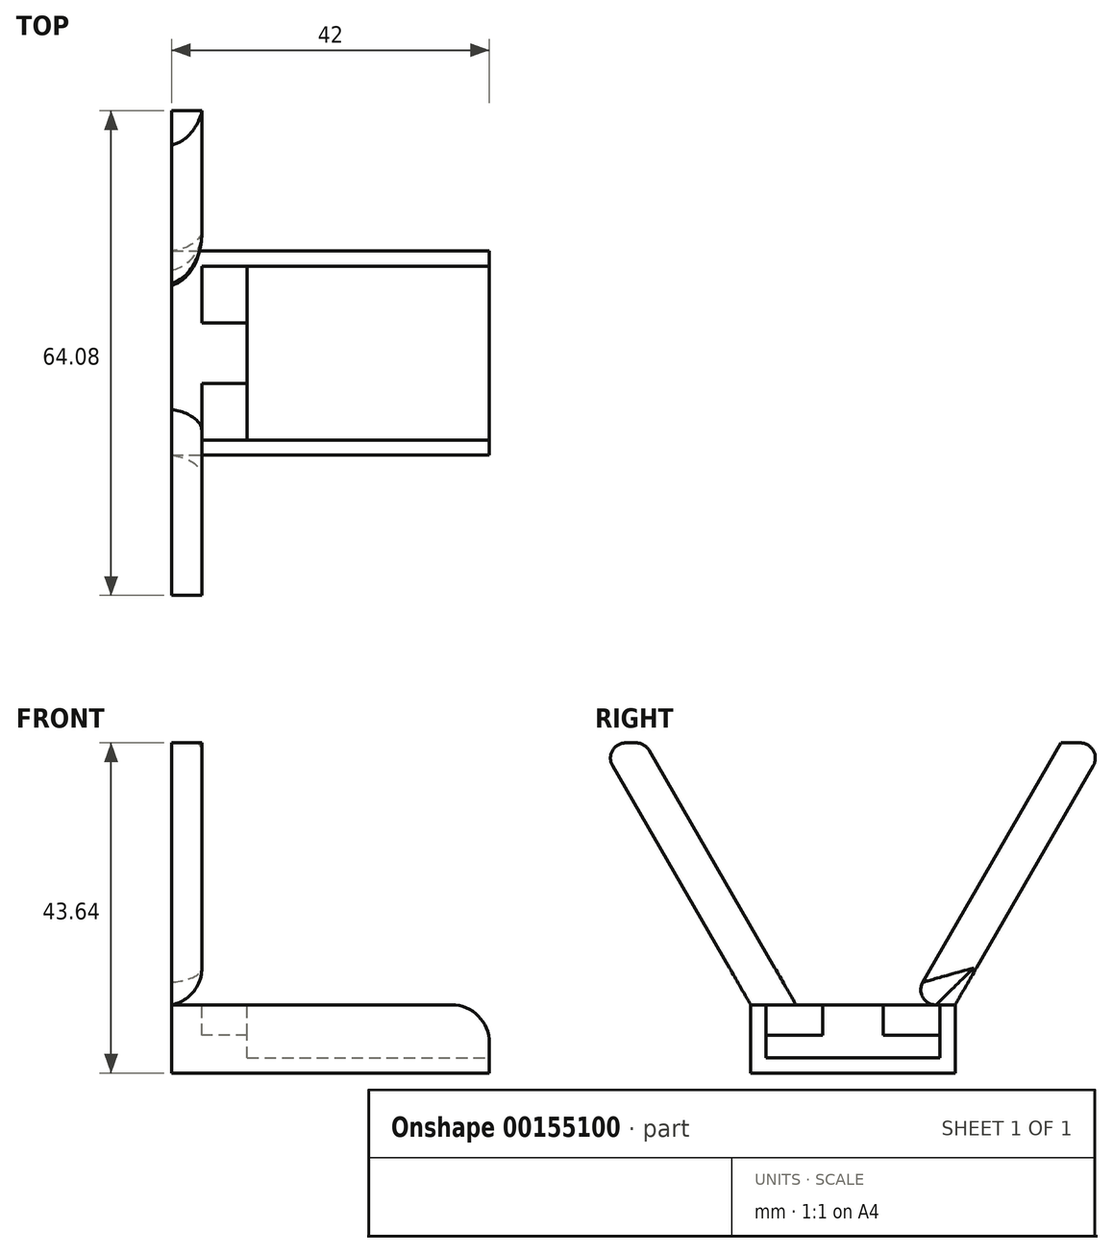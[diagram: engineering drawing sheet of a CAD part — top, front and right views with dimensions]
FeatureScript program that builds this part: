
annotation { "Feature Type Name" : "Feature", "Feature Type Description" : "" }
export const myFeature = defineFeature(function(context is Context, id is Id, definition is map)
    precondition{}
    {
        {
            var Q0;
            Q0=qCreatedBy(makeId("Top.planeOp"),FACE);
            var sketch = newSketch(context, id + "F0", { "sketchPlane" : qUnion([Q0])});
            skLineSegment(sketch, "E0.bottom", {"start": v(-21, 13.5) * mm, "end": v(21, 13.5) * mm});
            skLineSegment(sketch, "E0.top", {"start": v(-21, -13.5) * mm, "end": v(21, -13.5) * mm});
            skLineSegment(sketch, "E0.left", {"start": v(-21, 13.5) * mm, "end": v(-21, -13.5) * mm});
            skLineSegment(sketch, "E0.right", {"start": v(21, 13.5) * mm, "end": v(21, -13.5) * mm});
            skSolve(sketch);
        }
        {
            var Q0;
            Q0=qSketchRegion(id+"F0",true);
            extrude(context, id + "F1", {"entities" : qUnion([Q0]), "oppositeDirection" : true, "depth" : 9 * mm});
        }
        {
            var Q0;
            Q0=qCreatedBy(makeId("Top.planeOp"),FACE);
            var sketch = newSketch(context, id + "F2", { "sketchPlane" : qUnion([Q0])});
            skLineSegment(sketch, "E1.bottom", {"start": v(-11, 11.5) * mm, "end": v(21, 11.5) * mm});
            skLineSegment(sketch, "E1.top", {"start": v(-11, -11.5) * mm, "end": v(21, -11.5) * mm});
            skLineSegment(sketch, "E1.left", {"start": v(-11, 11.5) * mm, "end": v(-11, -11.5) * mm});
            skLineSegment(sketch, "E1.right", {"start": v(21, 11.5) * mm, "end": v(21, -11.5) * mm});
            skSolve(sketch);
        }
        {
            var Q0;
            Q0=qSketchRegion(id+"F2",true);
            extrude(context, id + "F3", {"entities" : qUnion([Q0]), "oppositeDirection" : true, "depth" : 7 * mm});
        }
        {
            var Q0;
            Q0=makeQuery(id+"F3.opExtrude","SWEPT_BODY",BODY,{"disambiguationData":[OSD([sQuery(id+"F2.wireOp",EDGE,"E1.bottom"),sQuery(id+"F2.wireOp",EDGE,"E1.top"),sQuery(id+"F2.wireOp",EDGE,"E1.left"),sQuery(id+"F2.wireOp",EDGE,"E1.right")])]});
            var Q1;
            Q1=makeQuery(id+"F1.opExtrude","SWEPT_BODY",BODY,{"disambiguationData":[OSD([sQuery(id+"F0.wireOp",EDGE,"E0.bottom"),sQuery(id+"F0.wireOp",EDGE,"E0.top"),sQuery(id+"F0.wireOp",EDGE,"E0.left"),sQuery(id+"F0.wireOp",EDGE,"E0.right")])]});
            booleanBodies(context, id + "F4", {"operationType" : BooleanOperationType.SUBTRACTION, "tools" : qUnion([Q0]), "targets" : qUnion([Q1])});
        }
        {
            var Q0;
            Q0=qCreatedBy(makeId("Top.planeOp"),FACE);
            var sketch = newSketch(context, id + "F5", { "sketchPlane" : qUnion([Q0])});
            skLineSegment(sketch, "E2.bottom", {"start": v(-11, 11.5) * mm, "end": v(-17, 11.5) * mm});
            skLineSegment(sketch, "E2.top", {"start": v(-11, 4) * mm, "end": v(-17, 4) * mm});
            skLineSegment(sketch, "E2.left", {"start": v(-11, 11.5) * mm, "end": v(-11, 4) * mm});
            skLineSegment(sketch, "E2.right", {"start": v(-17, 11.5) * mm, "end": v(-17, 4) * mm});
            skSolve(sketch);
        }
        {
            var Q0;
            Q0=qCreatedBy(makeId("Top.planeOp"),FACE);
            var sketch = newSketch(context, id + "F6", { "sketchPlane" : qUnion([Q0])});
            skLineSegment(sketch, "E3.bottom", {"start": v(-11, -4) * mm, "end": v(-17, -4) * mm});
            skLineSegment(sketch, "E3.top", {"start": v(-11, -11.5) * mm, "end": v(-17, -11.5) * mm});
            skLineSegment(sketch, "E3.left", {"start": v(-11, -4) * mm, "end": v(-11, -11.5) * mm});
            skLineSegment(sketch, "E3.right", {"start": v(-17, -4) * mm, "end": v(-17, -11.5) * mm});
            skSolve(sketch);
        }
        {
            var Q0;
            Q0=qSketchRegion(id+"F6",true);
            var Q1;
            Q1=qSketchRegion(id+"F5",true);
            extrude(context, id + "F7", {"entities" : qUnion([Q0, Q1]), "oppositeDirection" : true, "depth" : 4 * mm});
        }
        {
            var Q0;
            Q0=makeQuery(id+"F7.opExtrude","SWEPT_BODY",BODY,{"disambiguationData":[OSD([sQuery(id+"F5.wireOp",EDGE,"E2.bottom"),sQuery(id+"F5.wireOp",EDGE,"E2.top"),sQuery(id+"F5.wireOp",EDGE,"E2.left"),sQuery(id+"F5.wireOp",EDGE,"E2.right")])]});
            var Q1;
            Q1=makeQuery(id+"F7.opExtrude","SWEPT_BODY",BODY,{"disambiguationData":[OSD([sQuery(id+"F6.wireOp",EDGE,"E3.bottom"),sQuery(id+"F6.wireOp",EDGE,"E3.top"),sQuery(id+"F6.wireOp",EDGE,"E3.left"),sQuery(id+"F6.wireOp",EDGE,"E3.right")])]});
            var Q2;
            Q2=makeQuery(id+"F1.opExtrude","SWEPT_BODY",BODY,{"disambiguationData":[OSD([sQuery(id+"F0.wireOp",EDGE,"E0.bottom"),sQuery(id+"F0.wireOp",EDGE,"E0.top"),sQuery(id+"F0.wireOp",EDGE,"E0.left"),sQuery(id+"F0.wireOp",EDGE,"E0.right")])]});
            booleanBodies(context, id + "F8", {"operationType" : BooleanOperationType.SUBTRACTION, "tools" : qUnion([Q0, Q1]), "targets" : qUnion([Q2])});
        }
        {
            var Q0;
            Q0=makeQuery(id+"F1.opExtrude","SWEPT_FACE",FACE,{"disambiguationData":[OSD([sQuery(id+"F0.wireOp",EDGE,"E0.left")])]});
            var sketch = newSketch(context, id + "F9", { "sketchPlane" : qUnion([Q0])});
            skLineSegment(sketch, "E4", {"start": v(13.5, 0) * mm, "end": v(33.5, 34.64) * mm});
            skLineSegment(sketch, "E5", {"start": v(33.5, 34.64) * mm, "end": v(-33.5, 34.64) * mm});
            skLineSegment(sketch, "E6", {"start": v(-33.5, 34.64) * mm, "end": v(-13.5, 0) * mm});
            skLineSegment(sketch, "E7", {"start": v(-13.5, 0) * mm, "end": v(13.5, 0) * mm});
            skSolve(sketch);
        }
        {
            var Q0;
            Q0=qSketchRegion(id+"F9",true);
            extrude(context, id + "F10", {"entities" : qUnion([Q0]), "oppositeDirection" : true, "depth" : 4 * mm});
        }
        {
            var Q0;
            Q0=makeQuery(id+"F9.imprint","IMPRINT",FACE,{"disambiguationData":[TD([[makeQuery(id+"F9.imprint","IMPRINT",EDGE,{"derivedFrom":sQuery(id+"F9.wireOp",EDGE,"E4")}),1.0]])]});
            var sketch = newSketch(context, id + "F11", { "sketchPlane" : qUnion([Q0])});
            skLineSegment(sketch, "E8", {"start": v(7.5, 0) * mm, "end": v(27.5, 34.64) * mm});
            skLineSegment(sketch, "E9", {"start": v(27.5, 34.64) * mm, "end": v(-27.5, 34.64) * mm});
            skLineSegment(sketch, "E10", {"start": v(-27.5, 34.64) * mm, "end": v(-7.5, 0) * mm});
            skLineSegment(sketch, "E11", {"start": v(-7.5, 0) * mm, "end": v(7.5, 0) * mm});
            skSolve(sketch);
        }
        {
            var Q0;
            Q0=qSketchRegion(id+"F11",true);
            extrude(context, id + "F12", {"entities" : qUnion([Q0]), "oppositeDirection" : true, "depth" : 5 * mm});
        }
        {
            var Q0;
            Q0=makeQuery(id+"F12.opExtrude","SWEPT_BODY",BODY,{"disambiguationData":[OSD([sQuery(id+"F11.wireOp",EDGE,"E8"),sQuery(id+"F11.wireOp",EDGE,"E9"),sQuery(id+"F11.wireOp",EDGE,"E10"),sQuery(id+"F11.wireOp",EDGE,"E11")])]});
            var Q1;
            Q1=makeQuery(id+"F10.opExtrude","SWEPT_BODY",BODY,{"disambiguationData":[OSD([sQuery(id+"F9.wireOp",EDGE,"E4"),sQuery(id+"F9.wireOp",EDGE,"E5"),sQuery(id+"F9.wireOp",EDGE,"E6"),sQuery(id+"F9.wireOp",EDGE,"E7")])]});
            booleanBodies(context, id + "F13", {"operationType" : BooleanOperationType.SUBTRACTION, "tools" : qUnion([Q0]), "targets" : qUnion([Q1])});
        }
        {
            var Q0;
            Q0=makeQuery(id+"F10.opExtrude","SWEPT_EDGE",EDGE,{"disambiguationData":[OSD([sQuery(id+"F9.wireOp",EDGE,"E5"),sQuery(id+"F9.wireOp",EDGE,"E6")])]});
            var Q1;
            Q1=makeQuery(id+"F13.opBoolean","COPY",EDGE,{"derivedFrom":makeQuery(id+"F12.opExtrude","SWEPT_EDGE",EDGE,{"disambiguationData":[OSD([sQuery(id+"F9.wireOp",EDGE,"E5"),sQuery(id+"F11.wireOp",EDGE,"E9"),sQuery(id+"F11.wireOp",EDGE,"E10")])]})});
            var Q2;
            Q2=makeQuery(id+"F13.opBoolean","COPY",EDGE,{"derivedFrom":makeQuery(id+"F12.opExtrude","SWEPT_EDGE",EDGE,{"disambiguationData":[OSD([sQuery(id+"F9.wireOp",EDGE,"E5"),sQuery(id+"F11.wireOp",EDGE,"E8"),sQuery(id+"F11.wireOp",EDGE,"E9")])]})});
            var Q3;
            Q3=makeQuery(id+"F10.opExtrude","SWEPT_EDGE",EDGE,{"disambiguationData":[OSD([sQuery(id+"F9.wireOp",EDGE,"E4"),sQuery(id+"F9.wireOp",EDGE,"E5")])]});
            var Q4;
            Q4=makeQuery(id+"F13.opBoolean","COPY",EDGE,{"derivedFrom":makeQuery(id+"F12.opExtrude","SWEPT_EDGE",EDGE,{"disambiguationData":[OSD([sQuery(id+"F9.wireOp",EDGE,"E7"),sQuery(id+"F11.wireOp",EDGE,"E8"),sQuery(id+"F11.wireOp",EDGE,"E11")])]})});
            var Q5;
            Q5=makeQuery(id+"F13.opBoolean","COPY",EDGE,{"derivedFrom":makeQuery(id+"F12.opExtrude","SWEPT_EDGE",EDGE,{"disambiguationData":[OSD([sQuery(id+"F9.wireOp",EDGE,"E7"),sQuery(id+"F11.wireOp",EDGE,"E10"),sQuery(id+"F11.wireOp",EDGE,"E11")])]})});
            var Q6;
            Q6=makeQuery(id+"F4.opBoolean","COPY",EDGE,{"derivedFrom":makeQuery(id+"F3.opExtrude","CAP_EDGE",EDGE,{"disambiguationData":[OSD([sQuery(id+"F2.wireOp",EDGE,"E1.left")])],"isStart":true})});
            var Q7;
            Q7=makeQuery(id+"F8.opBoolean","COPY",EDGE,{"derivedFrom":makeQuery(id+"F7.opExtrude","CAP_EDGE",EDGE,{"disambiguationData":[OSD([sQuery(id+"F5.wireOp",EDGE,"E2.left")])],"isStart":false})});
            var Q8;
            Q8=makeQuery(id+"F8.opBoolean","COPY",EDGE,{"derivedFrom":makeQuery(id+"F7.opExtrude","CAP_EDGE",EDGE,{"disambiguationData":[OSD([sQuery(id+"F6.wireOp",EDGE,"E3.left")])],"isStart":false})});
            fillet(context, id + "F14", {"entities" : qUnion([Q0, Q1, Q2, Q3, Q4, Q5, Q6, Q7, Q8]), "radius" : 2 * mm, "tangentPropagation" : true, "allowEdgeOverflow" : false});
        }
        {
            var Q0;
            {var subQ0=sQuery(id+"F9.wireOp",EDGE,"E4");var subQ1=sQuery(id+"F9.wireOp",EDGE,"E7");Q0=makeQuery(id+"F13.opBoolean","SPLIT",EDGE,{"disambiguationData":[TD([makeQuery(id+"F10.opExtrude","SWEPT_FACE",FACE,{"disambiguationData":[OSD([subQ0])]})])],"derivedFrom":makeQuery(id+"F10.opExtrude","CAP_EDGE",EDGE,{"disambiguationData":[OSD([subQ1])],"isStart":false})});}
            var Q1;
            {var subQ0=sQuery(id+"F9.wireOp",EDGE,"E7");var subQ1=sQuery(id+"F9.wireOp",EDGE,"E6");Q1=makeQuery(id+"F13.opBoolean","SPLIT",EDGE,{"disambiguationData":[TD([makeQuery(id+"F10.opExtrude","SWEPT_FACE",FACE,{"disambiguationData":[OSD([subQ1])]})])],"derivedFrom":makeQuery(id+"F10.opExtrude","CAP_EDGE",EDGE,{"disambiguationData":[OSD([subQ0])],"isStart":false})});}
            var Q2;
            {var subQ0=sQuery(id+"F0.wireOp",EDGE,"E0.bottom");var subQ1=sQuery(id+"F0.wireOp",EDGE,"E0.right");Q2=makeQuery(id+"F4.opBoolean","SPLIT",EDGE,{"disambiguationData":[TD([makeQuery(id+"F1.opExtrude","SWEPT_FACE",FACE,{"disambiguationData":[OSD([subQ0])]})])],"derivedFrom":makeQuery(id+"F1.opExtrude","CAP_EDGE",EDGE,{"disambiguationData":[OSD([subQ1])],"isStart":true})});}
            var Q3;
            {var subQ0=sQuery(id+"F0.wireOp",EDGE,"E0.right");var subQ1=sQuery(id+"F0.wireOp",EDGE,"E0.top");Q3=makeQuery(id+"F4.opBoolean","SPLIT",EDGE,{"disambiguationData":[TD([makeQuery(id+"F1.opExtrude","SWEPT_FACE",FACE,{"disambiguationData":[OSD([subQ1])]})])],"derivedFrom":makeQuery(id+"F1.opExtrude","CAP_EDGE",EDGE,{"disambiguationData":[OSD([subQ0])],"isStart":true})});}
            fillet(context, id + "F15", {"entities" : qUnion([Q0, Q1, Q2, Q3]), "radius" : 5 * mm, "tangentPropagation" : true, "allowEdgeOverflow" : false});
        }
    });
